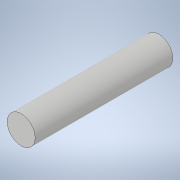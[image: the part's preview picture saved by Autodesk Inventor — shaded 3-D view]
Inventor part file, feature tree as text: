
AUTODESK INVENTOR PART (.ipt)
format: ipt  version: 2021 (Build 250183000, 183)  size: 91,648 bytes
history: native  units: mm
features: extrude x1
ambient origin geometry x8: Origin, YZ Plane, XZ Plane, XY Plane, X Axis, Y Axis, Z Axis, Center Point
bodies: Solid1 (feature_tree)
feature tree (1):
  extrude  "Extrusion1"  Depth=615.0mm TaperAngle=0.0deg
